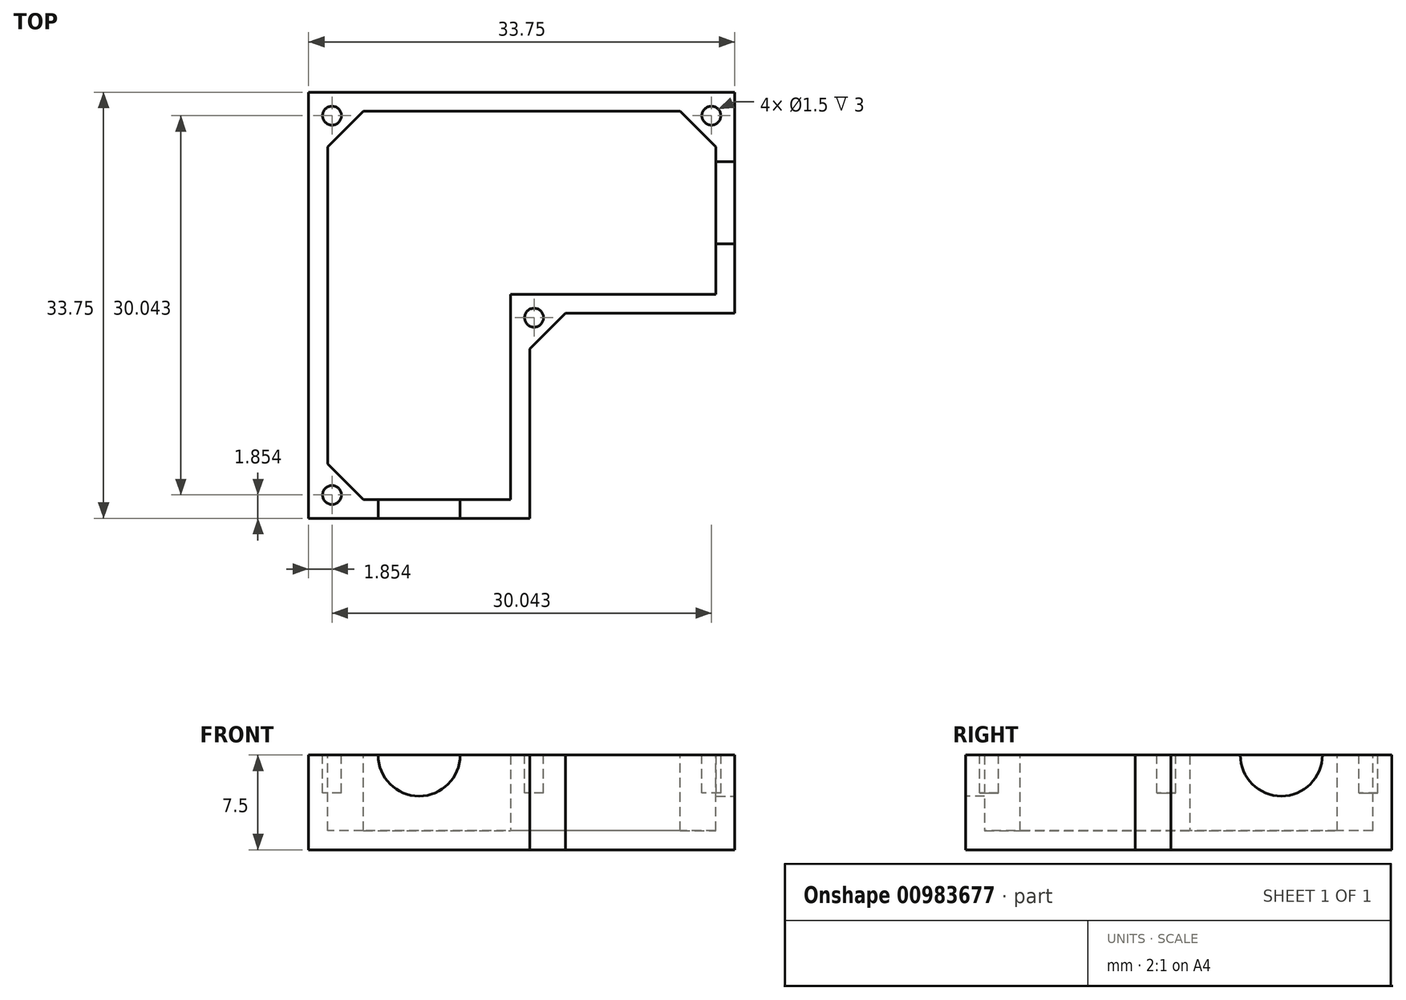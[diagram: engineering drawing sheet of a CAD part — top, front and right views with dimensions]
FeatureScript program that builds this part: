
annotation { "Feature Type Name" : "Feature", "Feature Type Description" : "" }
export const myFeature = defineFeature(function(context is Context, id is Id, definition is map)
    precondition{}
    {
        {
            var Q0;
            Q0=qCreatedBy(makeId("Top.planeOp"),FACE);
            var sketch = newSketch(context, id + "F0", { "sketchPlane" : qUnion([Q0])});
            skLineSegment(sketch, "E0.bottom", {"start": v(25, 8.75) * mm, "end": v(8.75, 8.75) * mm});
            skLineSegment(sketch, "E0.top", {"start": v(25, -8.75) * mm, "end": v(8.75, -8.75) * mm});
            skLineSegment(sketch, "E0.left", {"start": v(25, 8.75) * mm, "end": v(25, -8.75) * mm});
            skPoint(sketch, "E0.middle", {"position": v(0, 0) * mm});
            skLineSegment(sketch, "E1.top", {"start": v(-8.75, -25) * mm, "end": v(8.75, -25) * mm});
            skLineSegment(sketch, "E2.trimOffspring", {"start": v(-8.75, -8.75) * mm, "end": v(-8.75, -25) * mm});
            skLineSegment(sketch, "E3.trimOffspring", {"start": v(8.75, -8.75) * mm, "end": v(8.75, -25) * mm});
            skLineSegment(sketch, "E4", {"start": v(8.75, 8.75) * mm, "end": v(-8.75, 8.75) * mm});
            skLineSegment(sketch, "E5", {"start": v(-8.75, -8.75) * mm, "end": v(-8.75, 8.75) * mm});
            skLineSegment(sketch, "E6", {"start": v(0, 0) * mm, "end": v(0, -25) * mm});
            skLineSegment(sketch, "E7", {"start": v(0, 0) * mm, "end": v(25, 0) * mm});
            skLineSegment(sketch, "E8", {"start": v(0, 0) * mm, "end": v(-8.75, 0) * mm});
            skLineSegment(sketch, "E9", {"start": v(-8.75, 0) * mm, "end": v(0, 0) * mm});
            skLineSegment(sketch, "E10", {"start": v(0, 0) * mm, "end": v(0, 8.75) * mm});
            skSolve(sketch);
        }
        {
            var Q0;
            Q0=qSketchRegion(id+"F0",true);
            extrude(context, id + "F1", {"entities" : qUnion([Q0]), "depth" : 7.5 * mm, "offsetDistance" : 25 * mm});
        }
        {
            var Q0;
            Q0=makeQuery(id+"F1.opExtrude","CAP_FACE",FACE,{"disambiguationData":[OSD([sQuery(id+"F0.wireOp",EDGE,"E0.bottom"),sQuery(id+"F0.wireOp",EDGE,"E0.top"),sQuery(id+"F0.wireOp",EDGE,"E0.left"),sQuery(id+"F0.wireOp",EDGE,"E0.right"),sQuery(id+"F0.wireOp",EDGE,"E1.bottom"),sQuery(id+"F0.wireOp",EDGE,"E1.top"),sQuery(id+"F0.wireOp",EDGE,"E1.left"),sQuery(id+"F0.wireOp",EDGE,"E1.right"),sQuery(id+"F0.wireOp",EDGE,"1f207d6e-ecdf-4249-b46d-9234d2c6f181.trimOffspring"),sQuery(id+"F0.wireOp",EDGE,"E2.trimOffspring"),sQuery(id+"F0.wireOp",EDGE,"27587e5b-c096-4b03-bcea-66af693b9f10.trimOffspring"),sQuery(id+"F0.wireOp",EDGE,"E3.trimOffspring")])],"isStart":false});
            shell(context, id + "F2", {"entities" : qUnion([Q0]), "thickness" : 1.5 * mm});
        }
        {
            var Q0;
            Q0=makeQuery(id+"F1.opExtrude","CAP_FACE",FACE,{"disambiguationData":[OSD([sQuery(id+"F0.wireOp",EDGE,"E0.bottom"),sQuery(id+"F0.wireOp",EDGE,"E0.top"),sQuery(id+"F0.wireOp",EDGE,"E0.left"),sQuery(id+"F0.wireOp",EDGE,"E1.top"),sQuery(id+"F0.wireOp",EDGE,"E2.trimOffspring"),sQuery(id+"F0.wireOp",EDGE,"E3.trimOffspring"),sQuery(id+"F0.wireOp",EDGE,"E4"),sQuery(id+"F0.wireOp",EDGE,"E5")])],"isStart":false});
            var sketch = newSketch(context, id + "F3", { "sketchPlane" : qUnion([Q0])});
            skLineSegment(sketch, "E11", {"start": v(-7.25, 7.25) * mm, "end": v(-7.25, 4.42) * mm});
            skLineSegment(sketch, "E12", {"start": v(-7.25, 4.42) * mm, "end": v(-4.42, 7.25) * mm});
            skLineSegment(sketch, "E13", {"start": v(-4.42, 7.25) * mm, "end": v(-7.25, 7.25) * mm});
            skLineSegment(sketch, "E14", {"start": v(8.75, -8.75) * mm, "end": v(11.58, -8.75) * mm});
            skLineSegment(sketch, "E15", {"start": v(11.58, -8.75) * mm, "end": v(8.75, -11.58) * mm});
            skLineSegment(sketch, "E16", {"start": v(8.75, -11.58) * mm, "end": v(8.75, -8.75) * mm});
            skLineSegment(sketch, "E17", {"start": v(20.67, 7.25) * mm, "end": v(23.5, 4.42) * mm});
            skLineSegment(sketch, "E18", {"start": v(23.5, 4.42) * mm, "end": v(23.5, 7.25) * mm});
            skLineSegment(sketch, "E19", {"start": v(23.5, 7.25) * mm, "end": v(20.67, 7.25) * mm});
            skLineSegment(sketch, "E20", {"start": v(-7.25, -20.67) * mm, "end": v(-7.25, -23.5) * mm});
            skLineSegment(sketch, "E21", {"start": v(-7.25, -23.5) * mm, "end": v(-4.42, -23.5) * mm});
            skLineSegment(sketch, "E22", {"start": v(-4.42, -23.5) * mm, "end": v(-7.25, -20.67) * mm});
            skSolve(sketch);
        }
        {
            var Q0;
            Q0 = qSketchRegion(id + "F3", true);
            var Q1;
            Q1=makeQuery(id+"F1.opExtrude","CAP_FACE",FACE,{"disambiguationData":[OSD([sQuery(id+"F0.wireOp",EDGE,"E0.bottom"),sQuery(id+"F0.wireOp",EDGE,"E0.top"),sQuery(id+"F0.wireOp",EDGE,"E0.left"),sQuery(id+"F0.wireOp",EDGE,"E1.top"),sQuery(id+"F0.wireOp",EDGE,"E2.trimOffspring"),sQuery(id+"F0.wireOp",EDGE,"E3.trimOffspring"),sQuery(id+"F0.wireOp",EDGE,"E4"),sQuery(id+"F0.wireOp",EDGE,"E5")])],"isStart":true});
            extrude(context, id + "F4", {"entities" : qUnion([Q0]), "operationType" : NewBodyOperationType.ADD, "endBound" : BoundingType.UP_TO_SURFACE, "oppositeDirection" : true, "depth" : 25 * mm, "endBoundEntityFace" : qUnion([Q1]), "offsetDistance" : 25 * mm});
        }
        {
            var Q0;
            Q0=makeQuery(id+"F4.boolean.opBoolean","MERGE",FACE,{"derivedFrom":[makeQuery(id+"F1.opExtrude","CAP_FACE",FACE,{"disambiguationData":[OSD([sQuery(id+"F0.wireOp",EDGE,"E0.bottom"),sQuery(id+"F0.wireOp",EDGE,"E0.top"),sQuery(id+"F0.wireOp",EDGE,"E0.left"),sQuery(id+"F0.wireOp",EDGE,"E1.top"),sQuery(id+"F0.wireOp",EDGE,"E2.trimOffspring"),sQuery(id+"F0.wireOp",EDGE,"E3.trimOffspring"),sQuery(id+"F0.wireOp",EDGE,"E4"),sQuery(id+"F0.wireOp",EDGE,"E5")])],"isStart":false}),makeQuery(id+"F4.opExtrude","CAP_FACE",FACE,{"disambiguationData":[OSD([sQuery(id+"F3.wireOp",EDGE,"E11"),sQuery(id+"F3.wireOp",EDGE,"E12"),sQuery(id+"F3.wireOp",EDGE,"E13")])],"isStart":true}),makeQuery(id+"F4.opExtrude","CAP_FACE",FACE,{"disambiguationData":[OSD([sQuery(id+"F3.wireOp",EDGE,"E14"),sQuery(id+"F3.wireOp",EDGE,"E15"),sQuery(id+"F3.wireOp",EDGE,"E16")])],"isStart":true}),makeQuery(id+"F4.opExtrude","CAP_FACE",FACE,{"disambiguationData":[OSD([sQuery(id+"F3.wireOp",EDGE,"E17"),sQuery(id+"F3.wireOp",EDGE,"E18"),sQuery(id+"F3.wireOp",EDGE,"E19")])],"isStart":true}),makeQuery(id+"F4.opExtrude","CAP_FACE",FACE,{"disambiguationData":[OSD([sQuery(id+"F3.wireOp",EDGE,"E20"),sQuery(id+"F3.wireOp",EDGE,"E21"),sQuery(id+"F3.wireOp",EDGE,"E22")])],"isStart":true})]});
            var sketch = newSketch(context, id + "F5", { "sketchPlane" : qUnion([Q0])});
            skCircle(sketch, "E23", {"center": v(-6.9, 6.9) * mm, "radius": 0.75 * mm});
            skCircle(sketch, "E24", {"center": v(23.15, 6.9) * mm, "radius": 0.75 * mm});
            skCircle(sketch, "E25", {"center": v(9.1, -9.1) * mm, "radius": 0.75 * mm});
            skCircle(sketch, "E26", {"center": v(-6.9, -23.15) * mm, "radius": 0.75 * mm});
            skLineSegment(sketch, "E27", {"start": v(-6.9, 6.9) * mm, "end": v(-5.84, 5.84) * mm});
            skLineSegment(sketch, "E28", {"start": v(23.15, 6.9) * mm, "end": v(22.09, 5.84) * mm});
            skLineSegment(sketch, "E29", {"start": v(9.1, -9.1) * mm, "end": v(10.16, -10.16) * mm});
            skLineSegment(sketch, "E30", {"start": v(-6.9, -23.15) * mm, "end": v(-5.84, -22.09) * mm});
            skSolve(sketch);
        }
        {
            var Q0;
            Q0 = qSketchRegion(id + "F5", true);
            extrude(context, id + "F6", {"entities" : qUnion([Q0]), "operationType" : NewBodyOperationType.REMOVE, "oppositeDirection" : true, "depth" : 3 * mm, "offsetDistance" : 25 * mm});
        }
        {
            var Q0;
            Q0=makeQuery(id+"F1.opExtrude","SWEPT_FACE",FACE,{"disambiguationData":[OSD([sQuery(id+"F0.wireOp",EDGE,"E1.top")])]});
            var sketch = newSketch(context, id + "F7", { "sketchPlane" : qUnion([Q0])});
            skCircle(sketch, "E31", {"center": v(0, 7.5) * mm, "radius": 3.25 * mm});
            skSolve(sketch);
        }
        {
            var Q0;
            Q0 = qSketchRegion(id + "F7", true);
            var Q1;
            Q1=makeQuery(id+"F2.opShell","OFFSET_FACE",FACE,{"disambiguationData":[OSD([sQuery(id+"F0.wireOp",EDGE,"E0.bottom"),sQuery(id+"F0.wireOp",EDGE,"E4")])]});
            extrude(context, id + "F8", {"entities" : qUnion([Q0]), "operationType" : NewBodyOperationType.REMOVE, "endBound" : BoundingType.UP_TO_SURFACE, "oppositeDirection" : true, "depth" : 25 * mm, "endBoundEntityFace" : qUnion([Q1]), "offsetDistance" : 25 * mm});
        }
        {
            var Q0;
            Q0=makeQuery(id+"F1.opExtrude","SWEPT_FACE",FACE,{"disambiguationData":[OSD([sQuery(id+"F0.wireOp",EDGE,"E0.left")])]});
            var sketch = newSketch(context, id + "F9", { "sketchPlane" : qUnion([Q0])});
            skCircle(sketch, "E32", {"center": v(0, 7.5) * mm, "radius": 3.25 * mm});
            skSolve(sketch);
        }
        {
            var Q0;
            Q0 = qSketchRegion(id + "F9", true);
            var Q1;
            Q1=makeQuery(id+"F2.opShell","OFFSET_FACE",FACE,{"disambiguationData":[OSD([sQuery(id+"F0.wireOp",EDGE,"E2.trimOffspring"),sQuery(id+"F0.wireOp",EDGE,"E5")])]});
            extrude(context, id + "F10", {"entities" : qUnion([Q0]), "operationType" : NewBodyOperationType.REMOVE, "endBound" : BoundingType.UP_TO_SURFACE, "oppositeDirection" : true, "depth" : 25 * mm, "endBoundEntityFace" : qUnion([Q1]), "offsetDistance" : 25 * mm});
        }
    });
